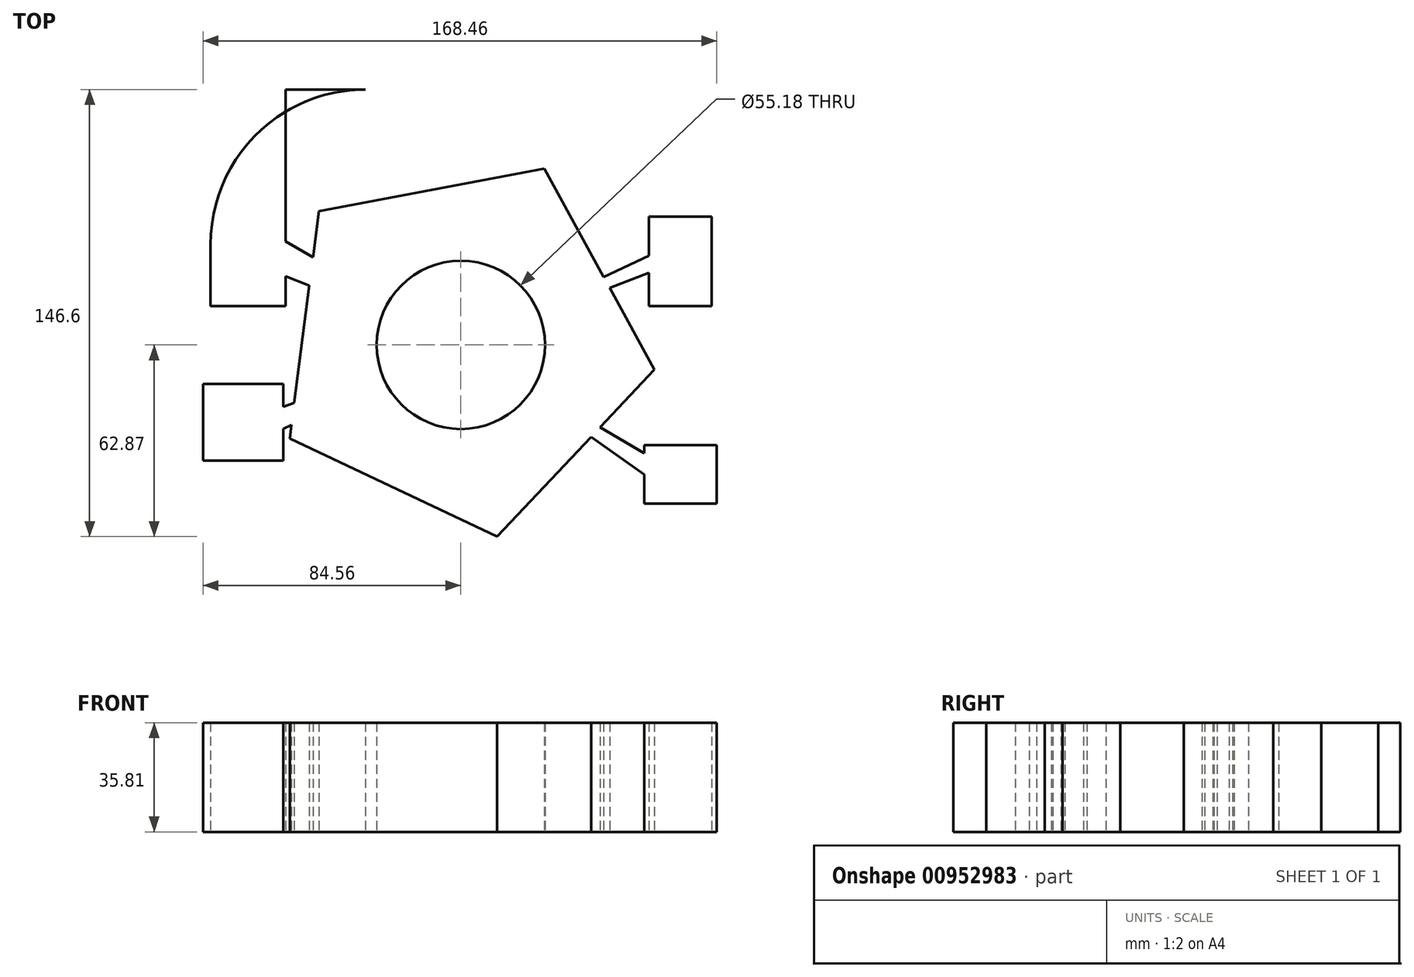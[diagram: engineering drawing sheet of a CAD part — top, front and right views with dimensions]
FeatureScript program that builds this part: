
annotation { "Feature Type Name" : "Feature", "Feature Type Description" : "" }
export const myFeature = defineFeature(function(context is Context, id is Id, definition is map)
    precondition{}
    {
        {
            var Q0;
            Q0=qCreatedBy(makeId("Top.planeOp"),FACE);
            var sketch = newSketch(context, id + "F0", { "sketchPlane" : qUnion([Q0])});
            skText(sketch, "E0", { "text": "martin", "fontName": "OpenSans-Bold.ttf"});
            skCircle(sketch, "E1", {"center": v(0, 0) * mm, "radius": 27.6 * mm});
            skCircle(sketch, "E2.cCircle", {"center": v(0, 0) * mm, "radius": 51.76 * mm, "construction": true});
            skLineSegment(sketch, "E2.0", {"start": v(27.36, 57.84) * mm, "end": v(63.46, -8.15) * mm});
            skLineSegment(sketch, "E2.1", {"start": v(63.46, -8.15) * mm, "end": v(11.86, -62.87) * mm});
            skLineSegment(sketch, "E2.2", {"start": v(11.86, -62.87) * mm, "end": v(-56.13, -30.71) * mm});
            skLineSegment(sketch, "E2.3", {"start": v(-56.13, -30.71) * mm, "end": v(-46.55, 43.9) * mm});
            skLineSegment(sketch, "E2.4", {"start": v(-46.55, 43.9) * mm, "end": v(27.36, 57.84) * mm});
            skPoint(sketch, "E2.0.midPoint", {"position": v(45.4, 24.85) * mm});
            skLineSegment(sketch, "E3", {"start": v(0, 0) * mm, "end": v(-14.7, 0) * mm});
            skLineSegment(sketch, "E4", {"start": v(-14.7, 0) * mm, "end": v(-51.76, 0) * mm});
            skLineSegment(sketch, "E5", {"start": v(-14.7, 0) * mm, "end": v(-27.6, 0) * mm});
            skLineSegment(sketch, "E6", {"start": v(-51.76, 0) * mm, "end": v(-52.43, -1.88) * mm});
            skLineSegment(sketch, "E7", {"start": v(-52.43, -1.88) * mm, "end": v(27.6, 0) * mm});
            skLineSegment(sketch, "E8", {"start": v(27.6, 0) * mm, "end": v(51.76, 0) * mm});
            skLineSegment(sketch, "E9", {"start": v(51.76, 0) * mm, "end": v(59, 0) * mm});
            skLineSegment(sketch, "E10", {"start": v(0, 0) * mm, "end": v(0.65, -27.58) * mm});
            skLineSegment(sketch, "E11", {"start": v(0.65, -27.58) * mm, "end": v(0.65, -51.76) * mm});
            skLineSegment(sketch, "E12", {"start": v(0.65, -51.76) * mm, "end": v(-0.11, -57.2) * mm});
            skLineSegment(sketch, "E13", {"start": v(-0.11, -57.2) * mm, "end": v(0, 0) * mm});
            skLineSegment(sketch, "E14", {"start": v(0, 0) * mm, "end": v(0, 27.6) * mm});
            skLineSegment(sketch, "E15", {"start": v(0, 27.6) * mm, "end": v(-0.57, 51.76) * mm});
            skLineSegment(sketch, "E16.bottom", {"start": v(-57.4, 83.73) * mm, "end": v(-31.29, 83.73) * mm});
            skLineSegment(sketch, "E16.top", {"start": v(-82.09, 12.72) * mm, "end": v(-57.4, 12.72) * mm});
            skLineSegment(sketch, "E16.left", {"start": v(-82.09, 32.93) * mm, "end": v(-82.09, 12.72) * mm});
            skLineSegment(sketch, "E16.right", {"start": v(-57.4, 83.73) * mm, "end": v(-57.4, 12.72) * mm});
            skLineSegment(sketch, "E17.bottom", {"start": v(-84.56, -12.85) * mm, "end": v(-58.2, -12.85) * mm});
            skLineSegment(sketch, "E17.top", {"start": v(-84.56, -37.9) * mm, "end": v(-58.2, -37.9) * mm});
            skLineSegment(sketch, "E17.left", {"start": v(-84.56, -12.85) * mm, "end": v(-84.56, -37.9) * mm});
            skLineSegment(sketch, "E17.right", {"start": v(-58.2, -12.85) * mm, "end": v(-58.2, -37.9) * mm});
            skLineSegment(sketch, "E18.bottom", {"start": v(61.62, 42.11) * mm, "end": v(82.18, 42.11) * mm});
            skLineSegment(sketch, "E18.top", {"start": v(61.62, 12.72) * mm, "end": v(82.18, 12.72) * mm});
            skLineSegment(sketch, "E18.left", {"start": v(61.62, 42.11) * mm, "end": v(61.62, 12.72) * mm});
            skLineSegment(sketch, "E18.right", {"start": v(82.18, 42.11) * mm, "end": v(82.18, 12.72) * mm});
            skLineSegment(sketch, "E19.bottom", {"start": v(60.17, -32.89) * mm, "end": v(83.9, -32.89) * mm});
            skLineSegment(sketch, "E19.top", {"start": v(60.17, -52) * mm, "end": v(83.9, -52) * mm});
            skLineSegment(sketch, "E19.left", {"start": v(60.17, -32.89) * mm, "end": v(60.17, -52) * mm});
            skLineSegment(sketch, "E19.right", {"start": v(83.9, -32.89) * mm, "end": v(83.9, -52) * mm});
            skPoint(sketch, "E20", {"position": v(-74.28, 29.2) * mm});
            skPoint(sketch, "E21", {"position": v(-71.11, -24.71) * mm});
            skPoint(sketch, "E22", {"position": v(72.83, 27.88) * mm});
            skPoint(sketch, "E23", {"position": v(71.9, -42.5) * mm});
            skLineSegment(sketch, "E24", {"start": v(-74.28, 29.2) * mm, "end": v(0, 0) * mm});
            skLineSegment(sketch, "E25", {"start": v(72.83, 27.88) * mm, "end": v(-0.11, 0) * mm});
            skLineSegment(sketch, "E26", {"start": v(71.9, -42.5) * mm, "end": v(0, 0) * mm});
            skLineSegment(sketch, "E27", {"start": v(-71.11, -24.71) * mm, "end": v(0, 0) * mm});
            skLineSegment(sketch, "E28", {"start": v(0, 0) * mm, "end": v(-57.4, 33.94) * mm});
            skLineSegment(sketch, "E29", {"start": v(0, 0) * mm, "end": v(61.62, 29.2) * mm});
            skLineSegment(sketch, "E30", {"start": v(-0.11, 0) * mm, "end": v(-58.2, -27.52) * mm});
            skLineSegment(sketch, "E31", {"start": v(0, 0) * mm, "end": v(60.17, -42.5) * mm});
            skPoint(sketch, "E32.visualSharp", {"position": v(-82.09, 83.73) * mm});
            skArc(sketch, "E32.filletArc", {"start": v(-31.29, 83.73) * mm, "mid": v(-67.2, 68.85) * mm, "end": v(-82.09, 32.93) * mm});
            const initialGuessF0  = {"E0": [-0.0147, -0.00613, 1, 0, 0.00613]};
            skSetInitialGuess(sketch, initialGuessF0);
            skSolve(sketch);
        }
        {
            var Q0;
            Q0 = qSketchRegion(id + "F0", true);
            extrude(context, id + "F1", {"entities" : qUnion([Q0]), "depth" : 35.81 * mm, "offsetDistance" : 25.4 * mm});
        }
    });
